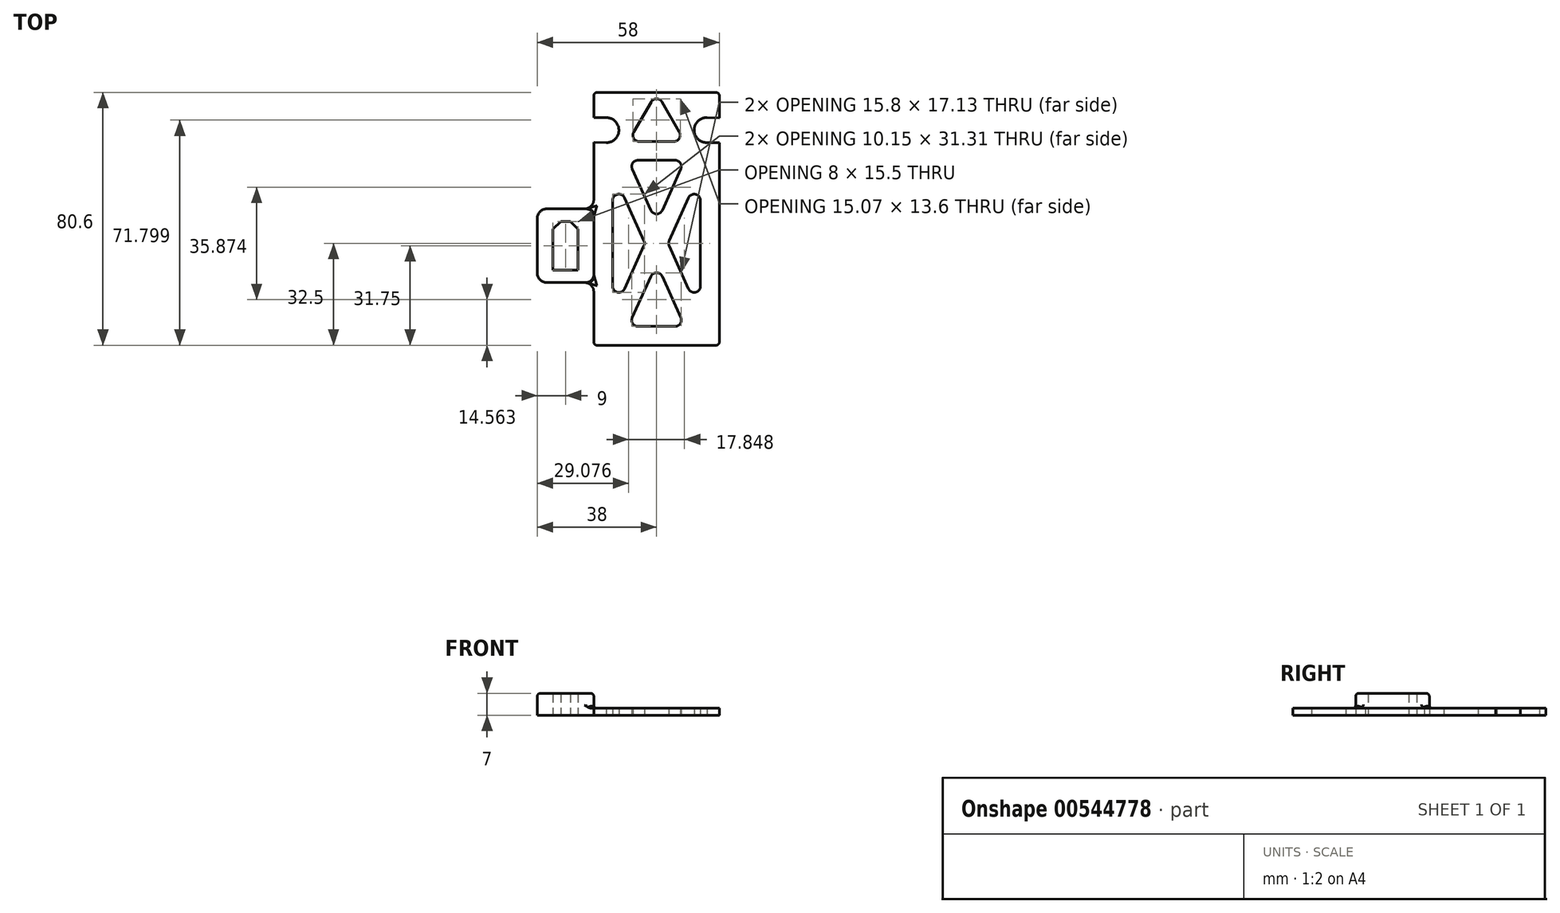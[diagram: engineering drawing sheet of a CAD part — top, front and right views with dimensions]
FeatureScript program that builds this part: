
annotation { "Feature Type Name" : "Feature", "Feature Type Description" : "" }
export const myFeature = defineFeature(function(context is Context, id is Id, definition is map)
    precondition{}
    {
        {
            var Q0;
            Q0=qCreatedBy(makeId("Top.planeOp"),FACE);
            var sketch = newSketch(context, id + "F0", { "sketchPlane" : qUnion([Q0])});
            skLineSegment(sketch, "E0.bottom", {"start": v(1, 0) * mm, "end": v(39, 0) * mm});
            skLineSegment(sketch, "E0.top", {"start": v(1, 80.6) * mm, "end": v(39, 80.6) * mm});
            skLineSegment(sketch, "E0.left", {"start": v(0, 43.5) * mm, "end": v(0, 79.6) * mm});
            skLineSegment(sketch, "E0.right", {"start": v(40, 1) * mm, "end": v(40, 79.6) * mm});
            skLineSegment(sketch, "E1", {"start": v(14.1, 6) * mm, "end": v(25.9, 6) * mm});
            skLineSegment(sketch, "E2", {"start": v(27.73, 8.82) * mm, "end": v(21.82, 21.95) * mm});
            skPoint(sketch, "E2.endSnap0", {"position": v(20, 6) * mm});
            skLineSegment(sketch, "E3", {"start": v(18.18, 21.95) * mm, "end": v(12.27, 8.82) * mm});
            skLineSegment(sketch, "E4", {"start": v(20, 0) * mm, "end": v(20, 80.6) * mm, "construction": true});
            skPoint(sketch, "E5.visualSharp", {"position": v(20, 26) * mm});
            skArc(sketch, "E5.filletArc", {"start": v(21.82, 21.95) * mm, "mid": v(20, 23.13) * mm, "end": v(18.18, 21.95) * mm});
            skPoint(sketch, "E6.visualSharp", {"position": v(11, 6) * mm});
            skArc(sketch, "E6.filletArc", {"start": v(12.27, 8.82) * mm, "mid": v(12.41, 6.91) * mm, "end": v(14.1, 6) * mm});
            skPoint(sketch, "E7.visualSharp", {"position": v(29, 6) * mm});
            skArc(sketch, "E7.filletArc", {"start": v(25.9, 6) * mm, "mid": v(27.59, 6.91) * mm, "end": v(27.73, 8.82) * mm});
            skLineSegment(sketch, "E8", {"start": v(14.1, 59) * mm, "end": v(25.9, 59) * mm});
            skLineSegment(sketch, "E9", {"start": v(27.73, 56.18) * mm, "end": v(21.82, 43.05) * mm});
            skLineSegment(sketch, "E10", {"start": v(18.18, 43.05) * mm, "end": v(12.27, 56.18) * mm});
            skPoint(sketch, "E11.visualSharp", {"position": v(11, 59) * mm});
            skArc(sketch, "E11.filletArc", {"start": v(14.1, 59) * mm, "mid": v(12.41, 58.09) * mm, "end": v(12.27, 56.18) * mm});
            skPoint(sketch, "E12.visualSharp", {"position": v(29, 59) * mm});
            skArc(sketch, "E12.filletArc", {"start": v(27.73, 56.18) * mm, "mid": v(27.59, 58.09) * mm, "end": v(25.9, 59) * mm});
            skPoint(sketch, "E13.visualSharp", {"position": v(20, 39) * mm});
            skArc(sketch, "E13.filletArc", {"start": v(18.18, 43.05) * mm, "mid": v(20, 41.87) * mm, "end": v(21.82, 43.05) * mm});
            skLineSegment(sketch, "E14", {"start": v(6, 46.17) * mm, "end": v(6, 18.83) * mm});
            skLineSegment(sketch, "E15", {"start": v(9.82, 18) * mm, "end": v(15.98, 31.68) * mm});
            skLineSegment(sketch, "E16", {"start": v(15.98, 33.32) * mm, "end": v(9.82, 47) * mm});
            skPoint(sketch, "E17.visualSharp", {"position": v(6, 55.49) * mm});
            skArc(sketch, "E17.filletArc", {"start": v(9.82, 47) * mm, "mid": v(7.58, 48.13) * mm, "end": v(6, 46.17) * mm});
            skPoint(sketch, "E18.visualSharp", {"position": v(6, 9.51) * mm});
            skArc(sketch, "E18.filletArc", {"start": v(6, 18.83) * mm, "mid": v(7.58, 16.87) * mm, "end": v(9.82, 18) * mm});
            skPoint(sketch, "E19.visualSharp", {"position": v(16.35, 32.5) * mm});
            skArc(sketch, "E19.filletArc", {"start": v(15.98, 31.68) * mm, "mid": v(16.15, 32.5) * mm, "end": v(15.98, 33.32) * mm});
            skArc(sketch, "E20.MirrorCS", {"start": v(34, 18.83) * mm, "mid": v(32.42, 16.87) * mm, "end": v(30.18, 18) * mm});
            skLineSegment(sketch, "E21.MirrorCS", {"start": v(30.18, 18) * mm, "end": v(24.02, 31.68) * mm});
            skArc(sketch, "E22.MirrorCS", {"start": v(30.18, 47) * mm, "mid": v(32.42, 48.13) * mm, "end": v(34, 46.17) * mm});
            skLineSegment(sketch, "E23.MirrorCS", {"start": v(34, 46.17) * mm, "end": v(34, 18.83) * mm});
            skLineSegment(sketch, "E24.MirrorCS", {"start": v(24.02, 33.32) * mm, "end": v(30.18, 47) * mm});
            skArc(sketch, "E25.MirrorCS", {"start": v(24.02, 31.68) * mm, "mid": v(23.85, 32.5) * mm, "end": v(24.02, 33.32) * mm});
            skLineSegment(sketch, "E26", {"start": v(14.46, 65) * mm, "end": v(25.54, 65) * mm});
            skPoint(sketch, "E27", {"position": v(20, 65) * mm});
            skLineSegment(sketch, "E28", {"start": v(12.73, 68) * mm, "end": v(18.27, 77.6) * mm});
            skLineSegment(sketch, "E29", {"start": v(27.27, 68) * mm, "end": v(21.73, 77.6) * mm});
            skPoint(sketch, "E30.visualSharp", {"position": v(11, 65) * mm});
            skArc(sketch, "E30.filletArc", {"start": v(12.73, 68) * mm, "mid": v(12.73, 66) * mm, "end": v(14.46, 65) * mm});
            skPoint(sketch, "E31.visualSharp", {"position": v(29, 65) * mm});
            skArc(sketch, "E31.filletArc", {"start": v(25.54, 65) * mm, "mid": v(27.27, 66) * mm, "end": v(27.27, 68) * mm});
            skPoint(sketch, "E32.visualSharp", {"position": v(20, 80.6) * mm});
            skArc(sketch, "E32.filletArc", {"start": v(21.73, 77.6) * mm, "mid": v(20, 78.6) * mm, "end": v(18.27, 77.6) * mm});
            skPoint(sketch, "E33.visualSharp", {"position": v(0, 80.6) * mm});
            skArc(sketch, "E33.filletArc", {"start": v(1, 80.6) * mm, "mid": v(0.3, 80.3) * mm, "end": v(0, 79.6) * mm});
            skPoint(sketch, "E34.visualSharp", {"position": v(40, 80.6) * mm});
            skArc(sketch, "E34.filletArc", {"start": v(40, 79.6) * mm, "mid": v(39.7, 80.3) * mm, "end": v(39, 80.6) * mm});
            skPoint(sketch, "E35.visualSharp", {"position": v(40, 0) * mm});
            skArc(sketch, "E35.filletArc", {"start": v(39, 0) * mm, "mid": v(39.7, 0.3) * mm, "end": v(40, 1) * mm});
            skPoint(sketch, "E36.visualSharp", {"position": v(0, 0) * mm});
            skArc(sketch, "E36.filletArc", {"start": v(0, 1) * mm, "mid": v(0.3, 0.3) * mm, "end": v(1, 0) * mm});
            skLineSegment(sketch, "E37.bottom", {"start": v(0, 20) * mm, "end": v(-18, 20) * mm});
            skLineSegment(sketch, "E37.top", {"start": v(0, 43.5) * mm, "end": v(-18, 43.5) * mm});
            skLineSegment(sketch, "E37.left", {"start": v(0, 20) * mm, "end": v(0, 43.5) * mm});
            skLineSegment(sketch, "E37.right", {"start": v(-18, 20) * mm, "end": v(-18, 43.5) * mm});
            skLineSegment(sketch, "E38.bottom", {"start": v(-13, 24) * mm, "end": v(-5, 24) * mm});
            skLineSegment(sketch, "E38.top", {"start": v(-10.5, 39.5) * mm, "end": v(-7.5, 39.5) * mm});
            skLineSegment(sketch, "E38.left", {"start": v(-13, 24) * mm, "end": v(-13, 37) * mm});
            skLineSegment(sketch, "E38.right", {"start": v(-5, 24) * mm, "end": v(-5, 37) * mm});
            skLineSegment(sketch, "E39", {"start": v(-13, 37) * mm, "end": v(-10.5, 39.5) * mm});
            skLineSegment(sketch, "E40", {"start": v(-5, 37) * mm, "end": v(-7.5, 39.5) * mm});
            skPoint(sketch, "E41.newPointA", {"position": v(0, 43.5) * mm});
            skLineSegment(sketch, "E42", {"start": v(0, 20) * mm, "end": v(0, 1) * mm});
            skLineSegment(sketch, "E43", {"start": v(-4.86, 68.6) * mm, "end": v(44.2, 68.6) * mm, "construction": true});
            skPoint(sketch, "E44", {"position": v(40, 68.6) * mm});
            skPoint(sketch, "E45", {"position": v(0, 68.6) * mm});
            skCircle(sketch, "E46", {"center": v(4, 68.6) * mm, "radius": 4 * mm});
            skCircle(sketch, "E47", {"center": v(36, 68.6) * mm, "radius": 4 * mm});
            skLineSegment(sketch, "E48", {"start": v(3.95, 72.6) * mm, "end": v(0, 72.6) * mm});
            skLineSegment(sketch, "E49", {"start": v(3.92, 64.6) * mm, "end": v(0, 64.68) * mm});
            skLineSegment(sketch, "E50", {"start": v(36.12, 72.6) * mm, "end": v(40, 72.48) * mm});
            skLineSegment(sketch, "E51", {"start": v(36.08, 64.6) * mm, "end": v(40, 64.6) * mm});
            skSolve(sketch);
        }
        {
            var Q0;
            Q0=makeQuery(id+"F0.imprint","IMPRINT",FACE,{"disambiguationData":[TD([[makeQuery(id+"F0.imprint","IMPRINT",EDGE,{"derivedFrom":sQuery(id+"F0.wireOp",EDGE,"E0.bottom")}),1.0]])]});
            var Q1;
            Q1=makeQuery(id+"F0.imprint","IMPRINT",FACE,{"disambiguationData":[TD([[makeQuery(id+"F0.imprint","IMPRINT",EDGE,{"derivedFrom":sQuery(id+"F0.wireOp",EDGE,"E37.bottom")}),-1.0]])]});
            extrude(context, id + "F1", {"entities" : qUnion([Q0, Q1]), "depth" : 2.2 * mm, "offsetDistance" : 25 * mm});
        }
        {
            var Q0;
            Q0=makeQuery(id+"F0.imprint","IMPRINT",FACE,{"disambiguationData":[TD([[makeQuery(id+"F0.imprint","IMPRINT",EDGE,{"derivedFrom":sQuery(id+"F0.wireOp",EDGE,"E37.bottom")}),-1.0]])]});
            extrude(context, id + "F2", {"entities" : qUnion([Q0]), "operationType" : NewBodyOperationType.ADD, "depth" : 7 * mm, "offsetDistance" : 25 * mm});
        }
        {
            var Q0;
            Q0=makeQuery(id+"F1.opExtrude","SWEPT_EDGE",EDGE,{"disambiguationData":[OSD([sQuery(id+"F0.wireOp",EDGE,"E0.left"),sQuery(id+"F0.wireOp",EDGE,"E37.top"),sQuery(id+"F0.wireOp",EDGE,"E37.left")])]});
            var Q1;
            Q1=makeQuery(id+"F1.opExtrude","SWEPT_EDGE",EDGE,{"disambiguationData":[OSD([sQuery(id+"F0.wireOp",EDGE,"E37.bottom"),sQuery(id+"F0.wireOp",EDGE,"E37.left"),sQuery(id+"F0.wireOp",EDGE,"E42")])]});
            var Q2;
            {var subQ0=sQuery(id+"F0.wireOp",EDGE,"E37.right");var subQ1=sQuery(id+"F0.wireOp",EDGE,"E37.top");Q2=makeQuery(id+"F2.boolean.opBoolean","MERGE",EDGE,{"derivedFrom":[makeQuery(id+"F1.opExtrude","SWEPT_EDGE",EDGE,{"disambiguationData":[OSD([subQ1,subQ0])]}),makeQuery(id+"F2.opExtrude","SWEPT_EDGE",EDGE,{"disambiguationData":[OSD([subQ1,subQ0])]})]});}
            var Q3;
            {var subQ0=sQuery(id+"F0.wireOp",EDGE,"E37.right");var subQ1=sQuery(id+"F0.wireOp",EDGE,"E37.bottom");Q3=makeQuery(id+"F2.boolean.opBoolean","MERGE",EDGE,{"derivedFrom":[makeQuery(id+"F1.opExtrude","SWEPT_EDGE",EDGE,{"disambiguationData":[OSD([subQ1,subQ0])]}),makeQuery(id+"F2.opExtrude","SWEPT_EDGE",EDGE,{"disambiguationData":[OSD([subQ1,subQ0])]})]});}
            fillet(context, id + "F3", {"entities" : qUnion([Q0, Q1, Q2, Q3]), "radius" : 3 * mm, "tangentPropagation" : true, "allowEdgeOverflow" : false});
        }
        {
            var Q0;
            Q0=makeQuery(id+"F2.boolean.opBoolean","INTERSECT",EDGE,{"derivedFrom":[makeQuery(id+"F1.opExtrude","CAP_FACE",FACE,{"disambiguationData":[OSD([sQuery(id+"F0.wireOp",EDGE,"E0.bottom"),sQuery(id+"F0.wireOp",EDGE,"E0.top"),sQuery(id+"F0.wireOp",EDGE,"E0.left"),sQuery(id+"F0.wireOp",EDGE,"E0.right"),sQuery(id+"F0.wireOp",EDGE,"E1"),sQuery(id+"F0.wireOp",EDGE,"E2"),sQuery(id+"F0.wireOp",EDGE,"E3"),sQuery(id+"F0.wireOp",EDGE,"E5.filletArc"),sQuery(id+"F0.wireOp",EDGE,"E6.filletArc"),sQuery(id+"F0.wireOp",EDGE,"E7.filletArc"),sQuery(id+"F0.wireOp",EDGE,"E8"),sQuery(id+"F0.wireOp",EDGE,"E9"),sQuery(id+"F0.wireOp",EDGE,"E10"),sQuery(id+"F0.wireOp",EDGE,"E11.filletArc"),sQuery(id+"F0.wireOp",EDGE,"E12.filletArc"),sQuery(id+"F0.wireOp",EDGE,"E13.filletArc"),sQuery(id+"F0.wireOp",EDGE,"E14"),sQuery(id+"F0.wireOp",EDGE,"E15"),sQuery(id+"F0.wireOp",EDGE,"E16"),sQuery(id+"F0.wireOp",EDGE,"E17.filletArc"),sQuery(id+"F0.wireOp",EDGE,"E18.filletArc"),sQuery(id+"F0.wireOp",EDGE,"E19.filletArc"),sQuery(id+"F0.wireOp",EDGE,"E20.MirrorCS"),sQuery(id+"F0.wireOp",EDGE,"E21.MirrorCS"),sQuery(id+"F0.wireOp",EDGE,"E22.MirrorCS"),sQuery(id+"F0.wireOp",EDGE,"E23.MirrorCS"),sQuery(id+"F0.wireOp",EDGE,"E24.MirrorCS"),sQuery(id+"F0.wireOp",EDGE,"E25.MirrorCS"),sQuery(id+"F0.wireOp",EDGE,"E26"),sQuery(id+"F0.wireOp",EDGE,"E28"),sQuery(id+"F0.wireOp",EDGE,"E29"),sQuery(id+"F0.wireOp",EDGE,"E30.filletArc"),sQuery(id+"F0.wireOp",EDGE,"E31.filletArc"),sQuery(id+"F0.wireOp",EDGE,"E32.filletArc"),sQuery(id+"F0.wireOp",EDGE,"E33.filletArc"),sQuery(id+"F0.wireOp",EDGE,"E34.filletArc"),sQuery(id+"F0.wireOp",EDGE,"E35.filletArc"),sQuery(id+"F0.wireOp",EDGE,"E36.filletArc"),sQuery(id+"F0.wireOp",EDGE,"E37.bottom"),sQuery(id+"F0.wireOp",EDGE,"E37.top"),sQuery(id+"F0.wireOp",EDGE,"E37.right"),sQuery(id+"F0.wireOp",EDGE,"E38.bottom"),sQuery(id+"F0.wireOp",EDGE,"E38.top"),sQuery(id+"F0.wireOp",EDGE,"E38.left"),sQuery(id+"F0.wireOp",EDGE,"E38.right"),sQuery(id+"F0.wireOp",EDGE,"E39"),sQuery(id+"F0.wireOp",EDGE,"E40"),sQuery(id+"F0.wireOp",EDGE,"E42")])],"isStart":false}),makeQuery(id+"F2.opExtrude","SWEPT_FACE",FACE,{"disambiguationData":[OSD([sQuery(id+"F0.wireOp",EDGE,"E37.left")])]})]});
            var Q1;
            Q1=makeQuery(id+"F2.opExtrude","CAP_EDGE",EDGE,{"disambiguationData":[OSD([sQuery(id+"F0.wireOp",EDGE,"E37.left")])],"isStart":false});
            var Q2;
            Q2=makeQuery(id+"F2.opExtrude","CAP_EDGE",EDGE,{"disambiguationData":[OSD([sQuery(id+"F0.wireOp",EDGE,"E37.bottom")])],"isStart":false});
            fillet(context, id + "F4", {"entities" : qUnion([Q0, Q1, Q2]), "radius" : 1 * mm, "tangentPropagation" : true, "allowEdgeOverflow" : false});
        }
        {
            var Q0;
            Q0=makeQuery(id+"F3.opFillet","TWEAK_EDGE",EDGE,{"derivedFrom":[makeQuery(id+"F1.opExtrude","CAP_VERTEX",VERTEX,{"disambiguationData":[OSD([sQuery(id+"F0.wireOp",EDGE,"E37.bottom"),sQuery(id+"F0.wireOp",EDGE,"E37.left"),sQuery(id+"F0.wireOp",EDGE,"E42")])],"isStart":false})]});
            var Q1;
            Q1=makeQuery(id+"F3.opFillet","TWEAK_EDGE",EDGE,{"derivedFrom":[makeQuery(id+"F1.opExtrude","CAP_VERTEX",VERTEX,{"disambiguationData":[OSD([sQuery(id+"F0.wireOp",EDGE,"E0.left"),sQuery(id+"F0.wireOp",EDGE,"E37.top"),sQuery(id+"F0.wireOp",EDGE,"E37.left")])],"isStart":false})]});
            fillet(context, id + "F5", {"entities" : qUnion([Q0, Q1]), "radius" : 1 * mm, "tangentPropagation" : true, "allowEdgeOverflow" : false});
        }
        {
            var Q0;
            Q0=makeQuery(id+"F2.opExtrude","SWEPT_EDGE",EDGE,{"disambiguationData":[OSD([sQuery(id+"F0.wireOp",EDGE,"E0.left"),sQuery(id+"F0.wireOp",EDGE,"E37.top"),sQuery(id+"F0.wireOp",EDGE,"E37.left")])]});
            var Q1;
            Q1=makeQuery(id+"F2.opExtrude","SWEPT_EDGE",EDGE,{"disambiguationData":[OSD([sQuery(id+"F0.wireOp",EDGE,"E37.bottom"),sQuery(id+"F0.wireOp",EDGE,"E37.left"),sQuery(id+"F0.wireOp",EDGE,"E42")])]});
            fillet(context, id + "F6", {"entities" : qUnion([Q0, Q1]), "radius" : 2.5 * mm, "tangentPropagation" : true, "allowEdgeOverflow" : false});
        }
    });
